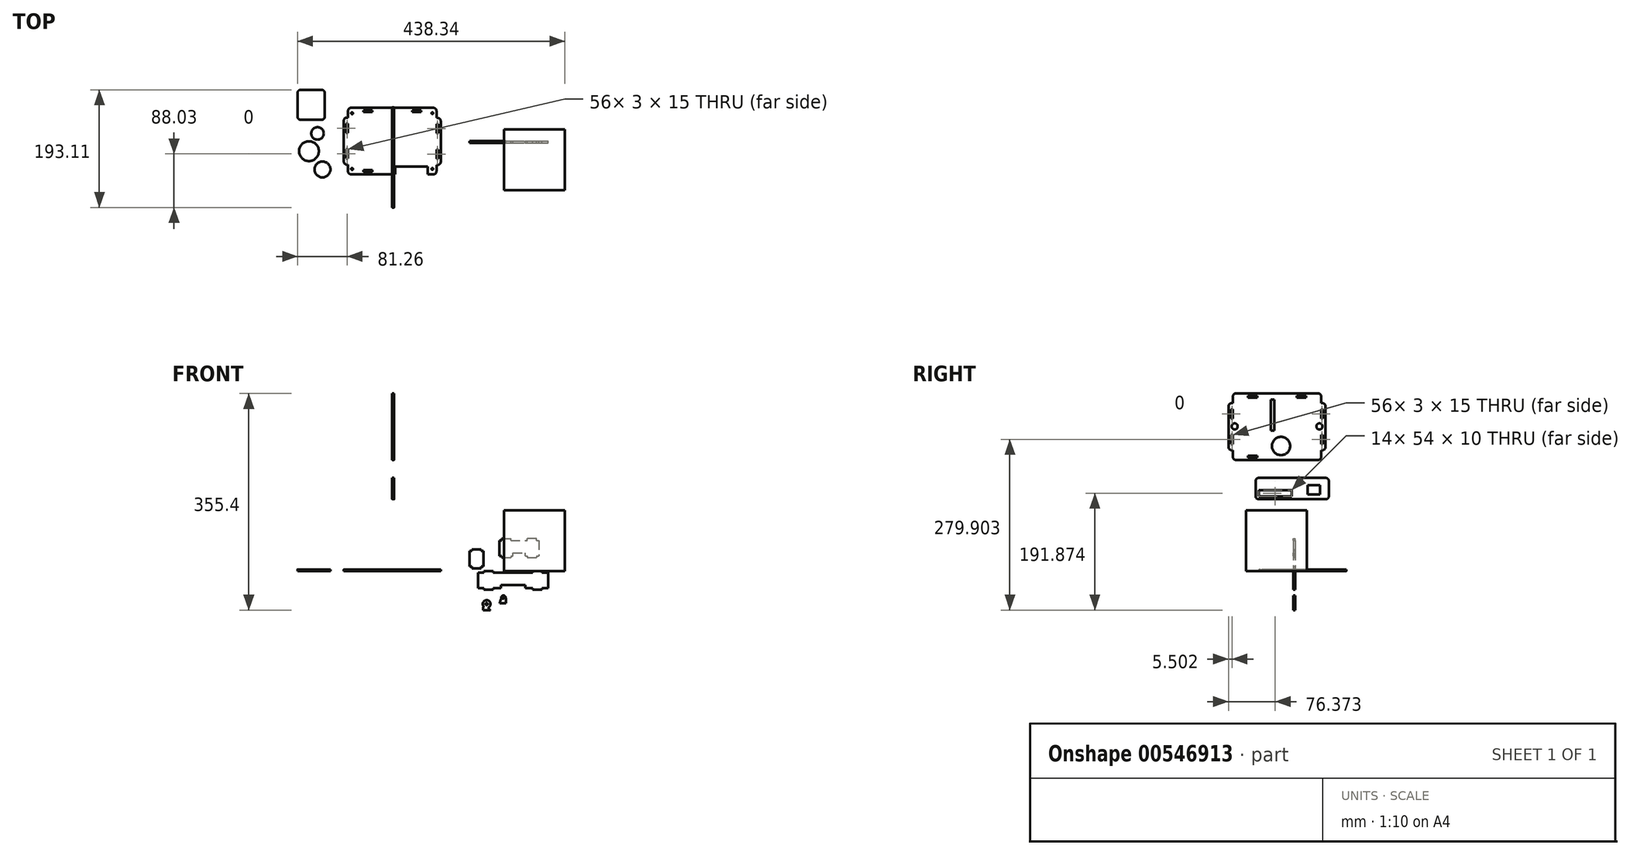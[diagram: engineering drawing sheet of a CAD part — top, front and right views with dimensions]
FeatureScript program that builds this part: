
annotation { "Feature Type Name" : "Feature", "Feature Type Description" : "" }
export const myFeature = defineFeature(function(context is Context, id is Id, definition is map)
    precondition{}
    {
        {
            var Q0;
            Q0=qCreatedBy(makeId("Top.planeOp"),FACE);
            var sketch = newSketch(context, id + "F0", { "sketchPlane" : qUnion([Q0])});
            skLineSegment(sketch, "E0.bottom", {"start": v(-72.5, 54.55) * mm, "end": v(72.5, 54.55) * mm});
            skLineSegment(sketch, "E0.top", {"start": v(-72.5, -54.55) * mm, "end": v(5.06, -54.55) * mm});
            skLineSegment(sketch, "E0.left", {"start": v(-72.5, 54.55) * mm, "end": v(-72.5, 38.5) * mm});
            skLineSegment(sketch, "E0.right", {"start": v(72.5, 54.55) * mm, "end": v(72.5, 37.9) * mm});
            skPoint(sketch, "E0.middle", {"position": v(0, 0) * mm});
            skLineSegment(sketch, "E1.bottom", {"start": v(-72.5, 38.5) * mm, "end": v(-79.5, 38.5) * mm});
            skLineSegment(sketch, "E1.top", {"start": v(-72.5, -38.5) * mm, "end": v(-79.5, -38.5) * mm});
            skLineSegment(sketch, "E1.right", {"start": v(-79.5, 38.5) * mm, "end": v(-79.5, -38.5) * mm});
            skCircle(sketch, "E2", {"center": v(-65.9, -45.8) * mm, "radius": 1.5 * mm});
            skCircle(sketch, "E3", {"center": v(65.9, -45.7) * mm, "radius": 1.5 * mm});
            skCircle(sketch, "E4", {"center": v(-65.9, 45.7) * mm, "radius": 1.5 * mm});
            skCircle(sketch, "E5", {"center": v(65.9, 45.8) * mm, "radius": 1.5 * mm});
            skLineSegment(sketch, "E6.bottom", {"start": v(5.06, -41.55) * mm, "end": v(58.06, -41.55) * mm});
            skLineSegment(sketch, "E6.left", {"start": v(5.06, -41.55) * mm, "end": v(5.06, -54.55) * mm});
            skLineSegment(sketch, "E6.right", {"start": v(58.06, -41.55) * mm, "end": v(58.06, -54.55) * mm});
            skLineSegment(sketch, "E7.bottom", {"start": v(-47.5, 50.55) * mm, "end": v(-32.5, 50.55) * mm});
            skLineSegment(sketch, "E7.top", {"start": v(-47.5, 47.55) * mm, "end": v(-32.5, 47.55) * mm});
            skLineSegment(sketch, "E7.left", {"start": v(-47.5, 50.55) * mm, "end": v(-47.5, 47.55) * mm});
            skLineSegment(sketch, "E7.right", {"start": v(-32.5, 50.55) * mm, "end": v(-32.5, 47.55) * mm});
            skLineSegment(sketch, "E8.bottom", {"start": v(32.5, 50.55) * mm, "end": v(47.5, 50.55) * mm});
            skLineSegment(sketch, "E8.top", {"start": v(32.5, 47.55) * mm, "end": v(47.5, 47.55) * mm});
            skLineSegment(sketch, "E8.left", {"start": v(32.5, 50.55) * mm, "end": v(32.5, 47.55) * mm});
            skLineSegment(sketch, "E8.right", {"start": v(47.5, 50.55) * mm, "end": v(47.5, 47.55) * mm});
            skLineSegment(sketch, "E9.bottom", {"start": v(-47.5, -47.55) * mm, "end": v(-32.5, -47.55) * mm});
            skLineSegment(sketch, "E9.top", {"start": v(-47.5, -50.55) * mm, "end": v(-32.5, -50.55) * mm});
            skLineSegment(sketch, "E9.left", {"start": v(-47.5, -47.55) * mm, "end": v(-47.5, -50.55) * mm});
            skLineSegment(sketch, "E9.right", {"start": v(-32.5, -47.55) * mm, "end": v(-32.5, -50.55) * mm});
            skLineSegment(sketch, "E10.bottom", {"start": v(79.5, 37.9) * mm, "end": v(72.5, 37.9) * mm});
            skLineSegment(sketch, "E10.top", {"start": v(79.5, -39.1) * mm, "end": v(72.5, -39.1) * mm});
            skLineSegment(sketch, "E10.left", {"start": v(79.5, 37.9) * mm, "end": v(79.5, -39.1) * mm});
            skLineSegment(sketch, "E11.trimOffspring", {"start": v(58.06, -54.55) * mm, "end": v(72.5, -54.55) * mm});
            skLineSegment(sketch, "E12.trimOffspring", {"start": v(72.5, -39.1) * mm, "end": v(72.5, -54.55) * mm});
            skLineSegment(sketch, "E13.trimOffspring", {"start": v(-72.5, -38.5) * mm, "end": v(-72.5, -54.55) * mm});
            skLineSegment(sketch, "E14.bottom", {"start": v(72.5, 27.9) * mm, "end": v(75.5, 27.9) * mm});
            skLineSegment(sketch, "E14.top", {"start": v(72.5, 12.9) * mm, "end": v(75.5, 12.9) * mm});
            skLineSegment(sketch, "E14.left", {"start": v(72.5, 27.9) * mm, "end": v(72.5, 12.9) * mm});
            skLineSegment(sketch, "E14.right", {"start": v(75.5, 27.9) * mm, "end": v(75.5, 12.9) * mm});
            skLineSegment(sketch, "E15.bottom", {"start": v(72.5, -14.1) * mm, "end": v(75.5, -14.1) * mm});
            skLineSegment(sketch, "E15.top", {"start": v(72.5, -29.1) * mm, "end": v(75.5, -29.1) * mm});
            skLineSegment(sketch, "E15.left", {"start": v(72.5, -14.1) * mm, "end": v(72.5, -29.1) * mm});
            skLineSegment(sketch, "E15.right", {"start": v(75.5, -14.1) * mm, "end": v(75.5, -29.1) * mm});
            skLineSegment(sketch, "E16.bottom", {"start": v(-75.5, 28.5) * mm, "end": v(-72.5, 28.5) * mm});
            skLineSegment(sketch, "E16.top", {"start": v(-75.5, 13.5) * mm, "end": v(-72.5, 13.5) * mm});
            skLineSegment(sketch, "E16.left", {"start": v(-75.5, 28.5) * mm, "end": v(-75.5, 13.5) * mm});
            skLineSegment(sketch, "E16.right", {"start": v(-72.5, 28.5) * mm, "end": v(-72.5, 13.5) * mm});
            skLineSegment(sketch, "E17.bottom", {"start": v(-75.5, -13.5) * mm, "end": v(-72.5, -13.5) * mm});
            skLineSegment(sketch, "E17.top", {"start": v(-75.5, -28.5) * mm, "end": v(-72.5, -28.5) * mm});
            skLineSegment(sketch, "E17.left", {"start": v(-75.5, -13.5) * mm, "end": v(-75.5, -28.5) * mm});
            skLineSegment(sketch, "E17.right", {"start": v(-72.5, -13.5) * mm, "end": v(-72.5, -28.5) * mm});
            skCircle(sketch, "E18", {"center": v(-136.53, -16.47) * mm, "radius": 16.26 * mm});
            skCircle(sketch, "E19", {"center": v(-122.54, 12.56) * mm, "radius": 10.27 * mm});
            skCircle(sketch, "E20", {"center": v(-114.36, -46.56) * mm, "radius": 13 * mm});
            skLineSegment(sketch, "E21.bottom", {"start": v(-155.26, 34.99) * mm, "end": v(-110.66, 34.99) * mm});
            skLineSegment(sketch, "E21.top", {"start": v(-155.26, 84.08) * mm, "end": v(-110.66, 84.08) * mm});
            skLineSegment(sketch, "E21.left", {"start": v(-155.26, 34.99) * mm, "end": v(-155.26, 84.08) * mm});
            skLineSegment(sketch, "E21.right", {"start": v(-110.66, 34.99) * mm, "end": v(-110.66, 84.08) * mm});
            skLineSegment(sketch, "E22.bottom", {"start": v(183.08, 19.36) * mm, "end": v(283.08, 19.36) * mm});
            skLineSegment(sketch, "E22.top", {"start": v(183.08, -80.64) * mm, "end": v(283.08, -80.64) * mm});
            skLineSegment(sketch, "E22.left", {"start": v(183.08, 19.36) * mm, "end": v(183.08, -80.64) * mm});
            skLineSegment(sketch, "E22.right", {"start": v(283.08, 19.36) * mm, "end": v(283.08, -80.64) * mm});
            skSolve(sketch);
        }
        {
            var Q0;
            Q0=qCreatedBy(makeId("Front.planeOp"),FACE);
            var sketch = newSketch(context, id + "F1", { "sketchPlane" : qUnion([Q0])});
            skLineSegment(sketch, "E23.bottom", {"start": v(130.57, 35.97) * mm, "end": v(145.57, 35.97) * mm});
            skLineSegment(sketch, "E23.top", {"start": v(130.57, 4.97) * mm, "end": v(145.57, 4.97) * mm});
            skLineSegment(sketch, "E23.left", {"start": v(130.57, 35.97) * mm, "end": v(130.57, 32.97) * mm});
            skLineSegment(sketch, "E23.right", {"start": v(145.57, 35.97) * mm, "end": v(145.57, 32.97) * mm});
            skLineSegment(sketch, "E24.bottom", {"start": v(126.57, 32.97) * mm, "end": v(130.57, 32.97) * mm});
            skLineSegment(sketch, "E24.top", {"start": v(126.57, 7.97) * mm, "end": v(130.57, 7.97) * mm});
            skLineSegment(sketch, "E24.left", {"start": v(126.57, 32.97) * mm, "end": v(126.57, 7.97) * mm});
            skLineSegment(sketch, "E24.right", {"start": v(149.57, 32.97) * mm, "end": v(149.57, 7.97) * mm});
            skLineSegment(sketch, "E25.trimOffspring", {"start": v(145.57, 32.97) * mm, "end": v(149.57, 32.97) * mm});
            skLineSegment(sketch, "E26.trimOffspring", {"start": v(145.57, 7.97) * mm, "end": v(149.57, 7.97) * mm});
            skLineSegment(sketch, "E27.trimOffspring", {"start": v(130.57, 7.97) * mm, "end": v(130.57, 4.97) * mm});
            skLineSegment(sketch, "E28.trimOffspring", {"start": v(145.57, 7.97) * mm, "end": v(145.57, 4.97) * mm});
            skLineSegment(sketch, "E29.bottom", {"start": v(140.54, -2.53) * mm, "end": v(150.54, -2.53) * mm});
            skLineSegment(sketch, "E29.top", {"start": v(140.54, -27.53) * mm, "end": v(150.54, -27.53) * mm});
            skLineSegment(sketch, "E29.left", {"start": v(140.54, -2.53) * mm, "end": v(140.54, -27.53) * mm});
            skLineSegment(sketch, "E29.right", {"start": v(255.54, -2.53) * mm, "end": v(255.54, -27.53) * mm});
            skLineSegment(sketch, "E30.top", {"start": v(150.54, 0.47) * mm, "end": v(165.54, 0.47) * mm});
            skLineSegment(sketch, "E30.left", {"start": v(150.54, -2.53) * mm, "end": v(150.54, 0.47) * mm});
            skLineSegment(sketch, "E30.right", {"start": v(165.54, -2.53) * mm, "end": v(165.54, 0.47) * mm});
            skLineSegment(sketch, "E31.top", {"start": v(230.54, 0.47) * mm, "end": v(245.54, 0.47) * mm});
            skLineSegment(sketch, "E31.left", {"start": v(230.54, -2.53) * mm, "end": v(230.54, 0.47) * mm});
            skLineSegment(sketch, "E31.right", {"start": v(245.54, -2.53) * mm, "end": v(245.54, 0.47) * mm});
            skLineSegment(sketch, "E32.top", {"start": v(150.54, -30.53) * mm, "end": v(165.54, -30.53) * mm});
            skLineSegment(sketch, "E32.left", {"start": v(150.54, -27.53) * mm, "end": v(150.54, -30.53) * mm});
            skLineSegment(sketch, "E32.right", {"start": v(165.54, -27.53) * mm, "end": v(165.54, -30.53) * mm});
            skLineSegment(sketch, "E33.top", {"start": v(230.54, -30.53) * mm, "end": v(245.54, -30.53) * mm});
            skLineSegment(sketch, "E33.left", {"start": v(230.54, -27.53) * mm, "end": v(230.54, -30.53) * mm});
            skLineSegment(sketch, "E33.right", {"start": v(245.54, -27.53) * mm, "end": v(245.54, -30.53) * mm});
            skLineSegment(sketch, "E34.bottom", {"start": v(194.44, 50.32) * mm, "end": v(197.94, 50.32) * mm});
            skLineSegment(sketch, "E34.top", {"start": v(194.44, 25.32) * mm, "end": v(197.94, 25.32) * mm});
            skLineSegment(sketch, "E35.top", {"start": v(179.44, 53.32) * mm, "end": v(194.44, 53.32) * mm});
            skLineSegment(sketch, "E35.left", {"start": v(179.44, 50.32) * mm, "end": v(179.44, 53.32) * mm});
            skLineSegment(sketch, "E35.right", {"start": v(194.44, 50.32) * mm, "end": v(194.44, 53.32) * mm});
            skLineSegment(sketch, "E36.top", {"start": v(179.44, 22.32) * mm, "end": v(194.44, 22.32) * mm});
            skLineSegment(sketch, "E36.left", {"start": v(179.44, 25.32) * mm, "end": v(179.44, 22.32) * mm});
            skLineSegment(sketch, "E36.right", {"start": v(194.44, 25.32) * mm, "end": v(194.44, 22.32) * mm});
            skLineSegment(sketch, "E37.top", {"start": v(221.44, 22.32) * mm, "end": v(236.44, 22.32) * mm});
            skLineSegment(sketch, "E37.left", {"start": v(221.44, 25.32) * mm, "end": v(221.44, 22.32) * mm});
            skLineSegment(sketch, "E37.right", {"start": v(236.44, 25.32) * mm, "end": v(236.44, 22.32) * mm});
            skLineSegment(sketch, "E38.top", {"start": v(236.44, 53.32) * mm, "end": v(221.44, 53.32) * mm});
            skLineSegment(sketch, "E38.left", {"start": v(236.44, 50.32) * mm, "end": v(236.44, 53.32) * mm});
            skLineSegment(sketch, "E38.right", {"start": v(221.44, 50.32) * mm, "end": v(221.44, 53.32) * mm});
            skLineSegment(sketch, "E39.bottom", {"start": v(179.44, 50.32) * mm, "end": v(175.44, 50.32) * mm});
            skLineSegment(sketch, "E39.top", {"start": v(179.44, 25.32) * mm, "end": v(175.44, 25.32) * mm});
            skLineSegment(sketch, "E39.right", {"start": v(175.44, 50.32) * mm, "end": v(175.44, 25.32) * mm});
            skLineSegment(sketch, "E40.bottom", {"start": v(236.44, 50.32) * mm, "end": v(240.44, 50.32) * mm});
            skLineSegment(sketch, "E40.top", {"start": v(236.44, 25.32) * mm, "end": v(240.44, 25.32) * mm});
            skLineSegment(sketch, "E40.right", {"start": v(240.44, 50.32) * mm, "end": v(240.44, 25.32) * mm});
            skLineSegment(sketch, "E41.top", {"start": v(178.04, -2.53) * mm, "end": v(218.04, -2.53) * mm});
            skLineSegment(sketch, "E41.left", {"start": v(178.04, -2.53) * mm, "end": v(178.04, -2.53) * mm});
            skLineSegment(sketch, "E41.right", {"start": v(218.04, -2.53) * mm, "end": v(218.04, -2.53) * mm});
            skLineSegment(sketch, "E42.top", {"start": v(178.04, -22.53) * mm, "end": v(218.04, -22.53) * mm});
            skLineSegment(sketch, "E42.left", {"start": v(178.04, -27.53) * mm, "end": v(178.04, -22.53) * mm});
            skLineSegment(sketch, "E42.right", {"start": v(218.04, -27.53) * mm, "end": v(218.04, -22.53) * mm});
            skLineSegment(sketch, "E43.top", {"start": v(197.94, 30.32) * mm, "end": v(217.94, 30.32) * mm});
            skLineSegment(sketch, "E43.left", {"start": v(197.94, 25.32) * mm, "end": v(197.94, 30.32) * mm});
            skLineSegment(sketch, "E43.right", {"start": v(217.94, 25.32) * mm, "end": v(217.94, 30.32) * mm});
            skLineSegment(sketch, "E44.top", {"start": v(197.94, 50.32) * mm, "end": v(217.94, 50.32) * mm});
            skLineSegment(sketch, "E44.left", {"start": v(197.94, 50.32) * mm, "end": v(197.94, 50.32) * mm});
            skLineSegment(sketch, "E44.right", {"start": v(217.94, 50.32) * mm, "end": v(217.94, 50.32) * mm});
            skLineSegment(sketch, "E45.trimOffspring", {"start": v(217.94, 50.32) * mm, "end": v(221.44, 50.32) * mm});
            skLineSegment(sketch, "E46.trimOffspring", {"start": v(218.04, -2.53) * mm, "end": v(230.54, -2.53) * mm});
            skLineSegment(sketch, "E47.trimOffspring", {"start": v(218.04, -27.53) * mm, "end": v(230.54, -27.53) * mm});
            skLineSegment(sketch, "E48.trimOffspring", {"start": v(217.94, 25.32) * mm, "end": v(221.44, 25.32) * mm});
            skLineSegment(sketch, "E49.trimOffspring", {"start": v(165.54, -27.53) * mm, "end": v(178.04, -27.53) * mm});
            skLineSegment(sketch, "E50.trimOffspring", {"start": v(165.54, -2.53) * mm, "end": v(178.04, -2.53) * mm});
            skLineSegment(sketch, "E51.trimOffspring", {"start": v(245.54, -27.53) * mm, "end": v(255.54, -27.53) * mm});
            skLineSegment(sketch, "E52.trimOffspring", {"start": v(245.54, -2.53) * mm, "end": v(255.54, -2.53) * mm});
            skLineSegment(sketch, "E53.bottom", {"start": v(148.76, -63.79) * mm, "end": v(160.76, -63.79) * mm});
            skArc(sketch, "E54", {"start": v(149.66, -57.6) * mm, "mid": v(148.98, -60.66) * mm, "end": v(148.76, -63.79) * mm});
            skArc(sketch, "E55", {"start": v(157.73, -59.41) * mm, "mid": v(158.82, -61.89) * mm, "end": v(160.76, -63.79) * mm});
            skArc(sketch, "E56", {"start": v(157.73, -59.41) * mm, "mid": v(156.15, -47.57) * mm, "end": v(149.66, -57.6) * mm});
            skCircle(sketch, "E57", {"center": v(154.76, -53.78) * mm, "radius": 1.75 * mm});
            skLineSegment(sketch, "E58.top", {"start": v(176.51, -52.41) * mm, "end": v(186.51, -52.41) * mm});
            skArc(sketch, "E59", {"start": v(178.98, -44.68) * mm, "mid": v(177.27, -48.4) * mm, "end": v(176.51, -52.41) * mm});
            skArc(sketch, "E60", {"start": v(185.6, -41.96) * mm, "mid": v(180.93, -40) * mm, "end": v(178.98, -44.68) * mm});
            skArc(sketch, "E61", {"start": v(186.51, -52.41) * mm, "mid": v(186.56, -47.14) * mm, "end": v(185.6, -41.96) * mm});
            skCircle(sketch, "E62", {"center": v(182.3, -43.32) * mm, "radius": 1.75 * mm});
            skSolve(sketch);
        }
        {
            var Q0;
            Q0=qCreatedBy(makeId("Right.planeOp"),FACE);
            var sketch = newSketch(context, id + "F2", { "sketchPlane" : qUnion([Q0])});
            skLineSegment(sketch, "E63.bottom", {"start": v(-102.03, 68.61) * mm, "end": v(42.97, 68.61) * mm});
            skLineSegment(sketch, "E63.top", {"start": v(-102.03, -40.39) * mm, "end": v(42.97, -40.39) * mm});
            skLineSegment(sketch, "E63.left", {"start": v(-102.03, 68.61) * mm, "end": v(-102.03, 52.61) * mm});
            skLineSegment(sketch, "E63.right", {"start": v(42.97, 68.61) * mm, "end": v(42.97, 52.61) * mm});
            skLineSegment(sketch, "E64.bottom", {"start": v(-109.03, 52.61) * mm, "end": v(-102.03, 52.61) * mm});
            skLineSegment(sketch, "E64.top", {"start": v(-109.03, -24.39) * mm, "end": v(-102.03, -24.39) * mm});
            skLineSegment(sketch, "E64.left", {"start": v(-109.03, 52.61) * mm, "end": v(-109.03, -24.39) * mm});
            skLineSegment(sketch, "E65.bottom", {"start": v(42.97, 52.61) * mm, "end": v(49.97, 52.61) * mm});
            skLineSegment(sketch, "E65.top", {"start": v(42.97, -24.39) * mm, "end": v(49.97, -24.39) * mm});
            skLineSegment(sketch, "E65.right", {"start": v(49.97, 52.61) * mm, "end": v(49.97, -24.39) * mm});
            skLineSegment(sketch, "E66.bottom", {"start": v(-40.03, 58.61) * mm, "end": v(-34.03, 58.61) * mm});
            skLineSegment(sketch, "E66.top", {"start": v(-40.03, 7.81) * mm, "end": v(-34.03, 7.81) * mm});
            skLineSegment(sketch, "E66.left", {"start": v(-40.03, 58.61) * mm, "end": v(-40.03, 7.81) * mm});
            skLineSegment(sketch, "E66.right", {"start": v(-34.03, 58.61) * mm, "end": v(-34.03, 7.81) * mm});
            skCircle(sketch, "E67", {"center": v(-23.03, -17.6) * mm, "radius": 15 * mm});
            skLineSegment(sketch, "E68.trimOffspring", {"start": v(-102.03, -24.39) * mm, "end": v(-102.03, -40.39) * mm});
            skLineSegment(sketch, "E69.trimOffspring", {"start": v(42.97, -24.39) * mm, "end": v(42.97, -40.39) * mm});
            skLineSegment(sketch, "E70.bottom", {"start": v(-77.03, 64.61) * mm, "end": v(-62.03, 64.61) * mm});
            skLineSegment(sketch, "E70.top", {"start": v(-77.03, 61.61) * mm, "end": v(-62.03, 61.61) * mm});
            skLineSegment(sketch, "E70.left", {"start": v(-77.03, 64.61) * mm, "end": v(-77.03, 61.61) * mm});
            skLineSegment(sketch, "E70.right", {"start": v(-62.03, 64.61) * mm, "end": v(-62.03, 61.61) * mm});
            skLineSegment(sketch, "E71.bottom", {"start": v(2.97, 64.61) * mm, "end": v(17.97, 64.61) * mm});
            skLineSegment(sketch, "E71.top", {"start": v(2.97, 61.61) * mm, "end": v(17.97, 61.61) * mm});
            skLineSegment(sketch, "E71.left", {"start": v(2.97, 64.61) * mm, "end": v(2.97, 61.61) * mm});
            skLineSegment(sketch, "E71.right", {"start": v(17.97, 64.61) * mm, "end": v(17.97, 61.61) * mm});
            skLineSegment(sketch, "E72.bottom", {"start": v(-105.03, 42.61) * mm, "end": v(-102.03, 42.61) * mm});
            skLineSegment(sketch, "E72.top", {"start": v(-105.03, 27.61) * mm, "end": v(-102.03, 27.61) * mm});
            skLineSegment(sketch, "E72.left", {"start": v(-105.03, 42.61) * mm, "end": v(-105.03, 27.61) * mm});
            skLineSegment(sketch, "E72.right", {"start": v(-102.03, 42.61) * mm, "end": v(-102.03, 27.61) * mm});
            skLineSegment(sketch, "E73.bottom", {"start": v(-105.03, 0.61) * mm, "end": v(-102.03, 0.61) * mm});
            skLineSegment(sketch, "E73.top", {"start": v(-105.03, -14.39) * mm, "end": v(-102.03, -14.39) * mm});
            skLineSegment(sketch, "E73.left", {"start": v(-105.03, 0.61) * mm, "end": v(-105.03, -14.39) * mm});
            skLineSegment(sketch, "E73.right", {"start": v(-102.03, 0.61) * mm, "end": v(-102.03, -14.39) * mm});
            skLineSegment(sketch, "E74.bottom", {"start": v(-77.03, -33.39) * mm, "end": v(-62.03, -33.39) * mm});
            skLineSegment(sketch, "E74.top", {"start": v(-77.03, -36.39) * mm, "end": v(-62.03, -36.39) * mm});
            skLineSegment(sketch, "E74.left", {"start": v(-77.03, -33.39) * mm, "end": v(-77.03, -36.39) * mm});
            skLineSegment(sketch, "E74.right", {"start": v(-62.03, -33.39) * mm, "end": v(-62.03, -36.39) * mm});
            skLineSegment(sketch, "E75.bottom", {"start": v(42.53, 42.61) * mm, "end": v(45.53, 42.61) * mm});
            skLineSegment(sketch, "E75.top", {"start": v(42.53, 27.61) * mm, "end": v(45.53, 27.61) * mm});
            skLineSegment(sketch, "E75.left", {"start": v(42.53, 42.61) * mm, "end": v(42.53, 27.61) * mm});
            skLineSegment(sketch, "E75.right", {"start": v(45.53, 42.61) * mm, "end": v(45.53, 27.61) * mm});
            skLineSegment(sketch, "E76.bottom", {"start": v(42.53, 0.61) * mm, "end": v(45.53, 0.61) * mm});
            skLineSegment(sketch, "E76.top", {"start": v(42.53, -14.39) * mm, "end": v(45.53, -14.39) * mm});
            skLineSegment(sketch, "E76.left", {"start": v(42.53, 0.61) * mm, "end": v(42.53, -14.39) * mm});
            skLineSegment(sketch, "E76.right", {"start": v(45.53, 0.61) * mm, "end": v(45.53, -14.39) * mm});
            skCircle(sketch, "E77", {"center": v(39.97, 14.61) * mm, "radius": 5 * mm});
            skCircle(sketch, "E78", {"center": v(-99.03, 14.61) * mm, "radius": 5 * mm});
            skSolve(sketch);
        }
        {
            var Q0;
            Q0 = qSketchRegion(id + "F2", true);
            extrude(context, id + "F3", {"entities" : qUnion([Q0]), "depth" : 3 * mm, "offsetDistance" : 25 * mm});
        }
        {
            var Q0;
            Q0=makeQuery(id+"F3.opExtrude","SWEPT_BODY",BODY,{"disambiguationData":[OSD([sQuery(id+"F2.wireOp",EDGE,"E63.bottom"),sQuery(id+"F2.wireOp",EDGE,"E63.top"),sQuery(id+"F2.wireOp",EDGE,"E63.left"),sQuery(id+"F2.wireOp",EDGE,"E63.right"),sQuery(id+"F2.wireOp",EDGE,"E64.bottom"),sQuery(id+"F2.wireOp",EDGE,"E64.top"),sQuery(id+"F2.wireOp",EDGE,"E64.left"),sQuery(id+"F2.wireOp",EDGE,"E65.bottom"),sQuery(id+"F2.wireOp",EDGE,"E65.top"),sQuery(id+"F2.wireOp",EDGE,"E65.right"),sQuery(id+"F2.wireOp",EDGE,"E66.bottom"),sQuery(id+"F2.wireOp",EDGE,"E66.top"),sQuery(id+"F2.wireOp",EDGE,"E66.left"),sQuery(id+"F2.wireOp",EDGE,"E66.right"),sQuery(id+"F2.wireOp",EDGE,"E67"),sQuery(id+"F2.wireOp",EDGE,"E68.trimOffspring"),sQuery(id+"F2.wireOp",EDGE,"E69.trimOffspring"),sQuery(id+"F2.wireOp",EDGE,"E70.bottom"),sQuery(id+"F2.wireOp",EDGE,"E70.top"),sQuery(id+"F2.wireOp",EDGE,"E70.left"),sQuery(id+"F2.wireOp",EDGE,"E70.right"),sQuery(id+"F2.wireOp",EDGE,"E71.bottom"),sQuery(id+"F2.wireOp",EDGE,"E71.top"),sQuery(id+"F2.wireOp",EDGE,"E71.left"),sQuery(id+"F2.wireOp",EDGE,"E71.right"),sQuery(id+"F2.wireOp",EDGE,"E72.bottom"),sQuery(id+"F2.wireOp",EDGE,"E72.top"),sQuery(id+"F2.wireOp",EDGE,"E72.left"),sQuery(id+"F2.wireOp",EDGE,"E72.right"),sQuery(id+"F2.wireOp",EDGE,"E73.bottom"),sQuery(id+"F2.wireOp",EDGE,"E73.top"),sQuery(id+"F2.wireOp",EDGE,"E73.left"),sQuery(id+"F2.wireOp",EDGE,"E73.right"),sQuery(id+"F2.wireOp",EDGE,"E74.bottom"),sQuery(id+"F2.wireOp",EDGE,"E74.top"),sQuery(id+"F2.wireOp",EDGE,"E74.left"),sQuery(id+"F2.wireOp",EDGE,"E74.right"),sQuery(id+"F2.wireOp",EDGE,"E75.bottom"),sQuery(id+"F2.wireOp",EDGE,"E75.top"),sQuery(id+"F2.wireOp",EDGE,"E75.left"),sQuery(id+"F2.wireOp",EDGE,"E75.right"),sQuery(id+"F2.wireOp",EDGE,"E76.bottom"),sQuery(id+"F2.wireOp",EDGE,"E76.top"),sQuery(id+"F2.wireOp",EDGE,"E76.left"),sQuery(id+"F2.wireOp",EDGE,"E76.right")])]});
            transform(context, id + "F4", {"entities" : qUnion([Q0]), "transformType" : TransformType.TRANSLATION_3D, "dx" : 0 * mm, "dy" : 0 * mm, "dz" : 223 * mm, "makeCopy" : false});
        }
        {
            var Q0;
            Q0=makeQuery(id+"F0.imprint","IMPRINT",FACE,{"disambiguationData":[TD([[makeQuery(id+"F0.imprint","IMPRINT",EDGE,{"derivedFrom":sQuery(id+"F0.wireOp",EDGE,"E0.bottom")}),-1.0]])]});
            extrude(context, id + "F5", {"entities" : qUnion([Q0]), "depth" : 3 * mm, "offsetDistance" : 25 * mm});
        }
        {
            var Q0;
            Q0 = qSketchRegion(id + "F1", true);
            extrude(context, id + "F6", {"entities" : qUnion([Q0]), "depth" : 3 * mm, "offsetDistance" : 25 * mm});
        }
        {
            var Q0;
            Q0=makeQuery(id+"F5.opExtrude","SWEPT_EDGE",EDGE,{"disambiguationData":[OSD([sQuery(id+"F0.wireOp",EDGE,"E0.bottom"),sQuery(id+"F0.wireOp",EDGE,"E0.left")])]});
            var Q1;
            Q1=makeQuery(id+"F5.opExtrude","SWEPT_EDGE",EDGE,{"disambiguationData":[OSD([sQuery(id+"F0.wireOp",EDGE,"E1.bottom"),sQuery(id+"F0.wireOp",EDGE,"E1.right")])]});
            var Q2;
            Q2=makeQuery(id+"F5.opExtrude","SWEPT_EDGE",EDGE,{"disambiguationData":[OSD([sQuery(id+"F0.wireOp",EDGE,"E1.top"),sQuery(id+"F0.wireOp",EDGE,"E1.right")])]});
            var Q3;
            Q3=makeQuery(id+"F5.opExtrude","SWEPT_EDGE",EDGE,{"disambiguationData":[OSD([sQuery(id+"F0.wireOp",EDGE,"E0.top"),sQuery(id+"F0.wireOp",EDGE,"E13.trimOffspring")])]});
            var Q4;
            Q4=makeQuery(id+"F5.opExtrude","SWEPT_EDGE",EDGE,{"disambiguationData":[OSD([sQuery(id+"F0.wireOp",EDGE,"E11.trimOffspring"),sQuery(id+"F0.wireOp",EDGE,"E12.trimOffspring")])]});
            var Q5;
            Q5=makeQuery(id+"F5.opExtrude","SWEPT_EDGE",EDGE,{"disambiguationData":[OSD([sQuery(id+"F0.wireOp",EDGE,"E10.top"),sQuery(id+"F0.wireOp",EDGE,"E10.left")])]});
            var Q6;
            Q6=makeQuery(id+"F5.opExtrude","SWEPT_EDGE",EDGE,{"disambiguationData":[OSD([sQuery(id+"F0.wireOp",EDGE,"E10.bottom"),sQuery(id+"F0.wireOp",EDGE,"E10.left")])]});
            var Q7;
            Q7=makeQuery(id+"F5.opExtrude","SWEPT_EDGE",EDGE,{"disambiguationData":[OSD([sQuery(id+"F0.wireOp",EDGE,"E0.bottom"),sQuery(id+"F0.wireOp",EDGE,"E0.right")])]});
            var Q8;
            Q8=makeQuery(id+"F3.opExtrude","SWEPT_EDGE",EDGE,{"disambiguationData":[OSD([sQuery(id+"F2.wireOp",EDGE,"E65.bottom"),sQuery(id+"F2.wireOp",EDGE,"E65.right")])]});
            var Q9;
            Q9=makeQuery(id+"F3.opExtrude","SWEPT_EDGE",EDGE,{"disambiguationData":[OSD([sQuery(id+"F2.wireOp",EDGE,"E63.bottom"),sQuery(id+"F2.wireOp",EDGE,"E63.right")])]});
            var Q10;
            Q10=makeQuery(id+"F3.opExtrude","SWEPT_EDGE",EDGE,{"disambiguationData":[OSD([sQuery(id+"F2.wireOp",EDGE,"E63.bottom"),sQuery(id+"F2.wireOp",EDGE,"E63.left")])]});
            var Q11;
            Q11=makeQuery(id+"F3.opExtrude","SWEPT_EDGE",EDGE,{"disambiguationData":[OSD([sQuery(id+"F2.wireOp",EDGE,"E64.bottom"),sQuery(id+"F2.wireOp",EDGE,"E64.left")])]});
            var Q12;
            Q12=makeQuery(id+"F3.opExtrude","SWEPT_EDGE",EDGE,{"disambiguationData":[OSD([sQuery(id+"F2.wireOp",EDGE,"E64.top"),sQuery(id+"F2.wireOp",EDGE,"E64.left")])]});
            var Q13;
            Q13=makeQuery(id+"F3.opExtrude","SWEPT_EDGE",EDGE,{"disambiguationData":[OSD([sQuery(id+"F2.wireOp",EDGE,"E63.top"),sQuery(id+"F2.wireOp",EDGE,"E68.trimOffspring")])]});
            var Q14;
            Q14=makeQuery(id+"F3.opExtrude","SWEPT_EDGE",EDGE,{"disambiguationData":[OSD([sQuery(id+"F2.wireOp",EDGE,"E63.top"),sQuery(id+"F2.wireOp",EDGE,"E69.trimOffspring")])]});
            var Q15;
            Q15=makeQuery(id+"F3.opExtrude","SWEPT_EDGE",EDGE,{"disambiguationData":[OSD([sQuery(id+"F2.wireOp",EDGE,"E65.top"),sQuery(id+"F2.wireOp",EDGE,"E65.right")])]});
            fillet(context, id + "F7", {"entities" : qUnion([Q0, Q1, Q2, Q3, Q4, Q5, Q6, Q7, Q8, Q9, Q10, Q11, Q12, Q13, Q14, Q15]), "radius" : 5 * mm, "tangentPropagation" : true, "allowEdgeOverflow" : false});
        }
        {
            var Q0;
            Q0=qCreatedBy(makeId("Right.planeOp"),FACE);
            var sketch = newSketch(context, id + "F8", { "sketchPlane" : qUnion([Q0])});
            skLineSegment(sketch, "E79.bottom", {"start": v(55.34, 153.08) * mm, "end": v(-64.66, 153.08) * mm});
            skLineSegment(sketch, "E79.top", {"start": v(55.34, 118.08) * mm, "end": v(-64.66, 118.08) * mm});
            skLineSegment(sketch, "E79.left", {"start": v(55.34, 153.08) * mm, "end": v(55.34, 118.08) * mm});
            skLineSegment(sketch, "E79.right", {"start": v(-64.66, 153.08) * mm, "end": v(-64.66, 118.08) * mm});
            skLineSegment(sketch, "E80.bottom", {"start": v(-5.66, 133.08) * mm, "end": v(-59.66, 133.08) * mm});
            skLineSegment(sketch, "E80.top", {"start": v(-5.66, 123.08) * mm, "end": v(-59.66, 123.08) * mm});
            skLineSegment(sketch, "E80.left", {"start": v(-5.66, 133.08) * mm, "end": v(-5.66, 123.08) * mm});
            skLineSegment(sketch, "E80.right", {"start": v(-59.66, 133.08) * mm, "end": v(-59.66, 123.08) * mm});
            skLineSegment(sketch, "E81.bottom", {"start": v(20.83, 141.08) * mm, "end": v(40.83, 141.08) * mm});
            skLineSegment(sketch, "E81.top", {"start": v(20.83, 126.08) * mm, "end": v(40.83, 126.08) * mm});
            skLineSegment(sketch, "E81.left", {"start": v(20.83, 141.08) * mm, "end": v(20.83, 126.08) * mm});
            skLineSegment(sketch, "E81.right", {"start": v(40.83, 141.08) * mm, "end": v(40.83, 126.08) * mm});
            skSolve(sketch);
        }
        {
            var Q0;
            Q0=makeQuery(id+"F8.imprint","IMPRINT",FACE,{"disambiguationData":[TD([[makeQuery(id+"F8.imprint","IMPRINT",EDGE,{"derivedFrom":sQuery(id+"F8.wireOp",EDGE,"E79.bottom")}),1.0]])]});
            extrude(context, id + "F9", {"entities" : qUnion([Q0]), "depth" : 3 * mm, "offsetDistance" : 25 * mm});
        }
        {
            var Q0;
            Q0=makeQuery(id+"F9.opExtrude","SWEPT_EDGE",EDGE,{"disambiguationData":[OSD([sQuery(id+"F8.wireOp",EDGE,"E79.top"),sQuery(id+"F8.wireOp",EDGE,"E79.right")])]});
            var Q1;
            Q1=makeQuery(id+"F9.opExtrude","SWEPT_EDGE",EDGE,{"disambiguationData":[OSD([sQuery(id+"F8.wireOp",EDGE,"E79.bottom"),sQuery(id+"F8.wireOp",EDGE,"E79.right")])]});
            var Q2;
            Q2=makeQuery(id+"F9.opExtrude","SWEPT_EDGE",EDGE,{"disambiguationData":[OSD([sQuery(id+"F8.wireOp",EDGE,"E79.bottom"),sQuery(id+"F8.wireOp",EDGE,"E79.left")])]});
            var Q3;
            Q3=makeQuery(id+"F9.opExtrude","SWEPT_EDGE",EDGE,{"disambiguationData":[OSD([sQuery(id+"F8.wireOp",EDGE,"E79.top"),sQuery(id+"F8.wireOp",EDGE,"E79.left")])]});
            fillet(context, id + "F10", {"entities" : qUnion([Q0, Q1, Q2, Q3]), "radius" : 5 * mm, "tangentPropagation" : true, "allowEdgeOverflow" : false});
        }
        {
            var Q0;
            Q0=makeQuery(id+"F0.imprint","IMPRINT",FACE,{"disambiguationData":[TD([[makeQuery(id+"F0.imprint","IMPRINT",EDGE,{"derivedFrom":sQuery(id+"F0.wireOp",EDGE,"E21.bottom")}),1.0]])]});
            extrude(context, id + "F11", {"entities" : qUnion([Q0]), "depth" : 3 * mm, "offsetDistance" : 25 * mm});
        }
        {
            var Q0;
            Q0=makeQuery(id+"F11.opExtrude","SWEPT_EDGE",EDGE,{"disambiguationData":[OSD([sQuery(id+"F0.wireOp",EDGE,"E21.bottom"),sQuery(id+"F0.wireOp",EDGE,"E21.right")])]});
            var Q1;
            Q1=makeQuery(id+"F11.opExtrude","SWEPT_EDGE",EDGE,{"disambiguationData":[OSD([sQuery(id+"F0.wireOp",EDGE,"E21.bottom"),sQuery(id+"F0.wireOp",EDGE,"E21.left")])]});
            var Q2;
            Q2=makeQuery(id+"F11.opExtrude","SWEPT_EDGE",EDGE,{"disambiguationData":[OSD([sQuery(id+"F0.wireOp",EDGE,"E21.top"),sQuery(id+"F0.wireOp",EDGE,"E21.left")])]});
            var Q3;
            Q3=makeQuery(id+"F11.opExtrude","SWEPT_EDGE",EDGE,{"disambiguationData":[OSD([sQuery(id+"F0.wireOp",EDGE,"E21.top"),sQuery(id+"F0.wireOp",EDGE,"E21.right")])]});
            fillet(context, id + "F12", {"entities" : qUnion([Q0, Q1, Q2, Q3]), "radius" : 5 * mm, "tangentPropagation" : true, "allowEdgeOverflow" : false});
        }
        {
            var Q0;
            Q0=makeQuery(id+"F0.imprint","IMPRINT",FACE,{"disambiguationData":[TD([[makeQuery(id+"F0.imprint","IMPRINT",EDGE,{"derivedFrom":sQuery(id+"F0.wireOp",EDGE,"E18")}),1.0]])]});
            extrude(context, id + "F13", {"entities" : qUnion([Q0]), "depth" : 3 * mm, "offsetDistance" : 25 * mm});
        }
        {
            var Q0;
            Q0=makeQuery(id+"F0.imprint","IMPRINT",FACE,{"disambiguationData":[TD([[makeQuery(id+"F0.imprint","IMPRINT",EDGE,{"derivedFrom":sQuery(id+"F0.wireOp",EDGE,"E19")}),1.0]])]});
            extrude(context, id + "F14", {"entities" : qUnion([Q0]), "depth" : 3 * mm, "offsetDistance" : 25 * mm});
        }
        {
            var Q0;
            Q0=makeQuery(id+"F0.imprint","IMPRINT",FACE,{"disambiguationData":[TD([[makeQuery(id+"F0.imprint","IMPRINT",EDGE,{"derivedFrom":sQuery(id+"F0.wireOp",EDGE,"E20")}),1.0]])]});
            extrude(context, id + "F15", {"entities" : qUnion([Q0]), "depth" : 3 * mm, "offsetDistance" : 25 * mm});
        }
        {
            var Q0;
            Q0=makeQuery(id+"F0.imprint","IMPRINT",FACE,{"disambiguationData":[TD([[makeQuery(id+"F0.imprint","IMPRINT",EDGE,{"derivedFrom":sQuery(id+"F0.wireOp",EDGE,"E22.bottom")}),-1.0]])]});
            extrude(context, id + "F16", {"entities" : qUnion([Q0]), "depth" : 100 * mm, "offsetDistance" : 25 * mm});
        }
    });
